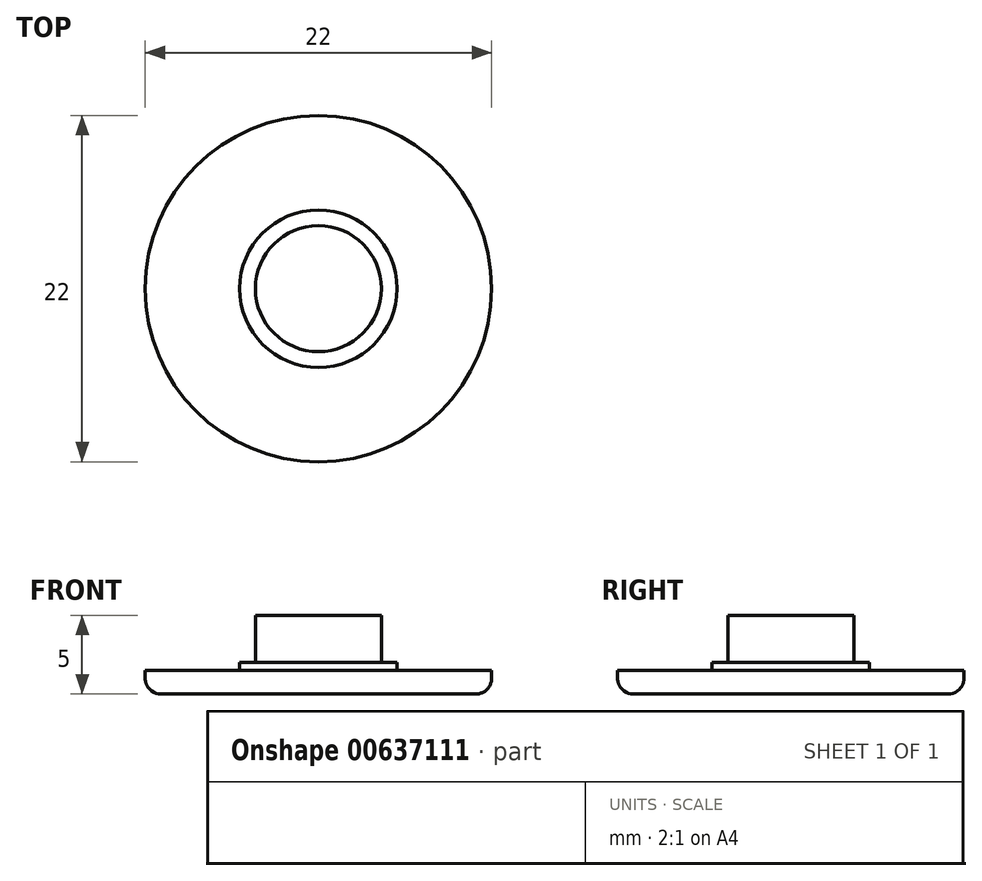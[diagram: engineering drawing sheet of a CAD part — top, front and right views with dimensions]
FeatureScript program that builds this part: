
annotation { "Feature Type Name" : "Feature", "Feature Type Description" : "" }
export const myFeature = defineFeature(function(context is Context, id is Id, definition is map)
    precondition{}
    {
        {
            var Q0;
            Q0=qCreatedBy(makeId("Top.planeOp"),FACE);
            var sketch = newSketch(context, id + "F0", { "sketchPlane" : qUnion([Q0])});
            skCircle(sketch, "E0", {"center": v(0, 0) * mm, "radius": 11 * mm});
            skCircle(sketch, "E1", {"center": v(0, 0) * mm, "radius": 4 * mm});
            skCircle(sketch, "E2", {"center": v(0, 0) * mm, "radius": 5 * mm});
            skSolve(sketch);
        }
        {
            var Q0;
            Q0=makeQuery(id+"F0.imprint","IMPRINT",FACE,{"disambiguationData":[TD([[makeQuery(id+"F0.imprint","IMPRINT",EDGE,{"derivedFrom":sQuery(id+"F0.wireOp",EDGE,"E0")}),1.0]])]});
            extrude(context, id + "F1", {"entities" : qUnion([Q0]), "depth" : 1.5 * mm, "offsetDistance" : 25 * mm});
        }
        {
            var Q0;
            Q0=makeQuery(id+"F0.imprint","IMPRINT",FACE,{"disambiguationData":[TD([[makeQuery(id+"F0.imprint","IMPRINT",EDGE,{"derivedFrom":sQuery(id+"F0.wireOp",EDGE,"E1")}),-1.0]])]});
            extrude(context, id + "F2", {"entities" : qUnion([Q0]), "operationType" : NewBodyOperationType.ADD, "depth" : 2 * mm, "offsetDistance" : 25 * mm});
        }
        {
            var Q0;
            Q0=makeQuery(id+"F0.imprint","IMPRINT",FACE,{"disambiguationData":[TD([[makeQuery(id+"F0.imprint","IMPRINT",EDGE,{"derivedFrom":sQuery(id+"F0.wireOp",EDGE,"E1")}),1.0]])]});
            extrude(context, id + "F3", {"entities" : qUnion([Q0]), "operationType" : NewBodyOperationType.ADD, "depth" : 5 * mm, "offsetDistance" : 25 * mm});
        }
        {
            var Q0;
            Q0=makeQuery(id+"F1.opExtrude","CAP_EDGE",EDGE,{"disambiguationData":[OSD([sQuery(id+"F0.wireOp",EDGE,"E0")])],"isStart":true});
            fillet(context, id + "F4", {"entities" : qUnion([Q0]), "radius" : 1 * mm, "tangentPropagation" : true, "allowEdgeOverflow" : false});
        }
    });
